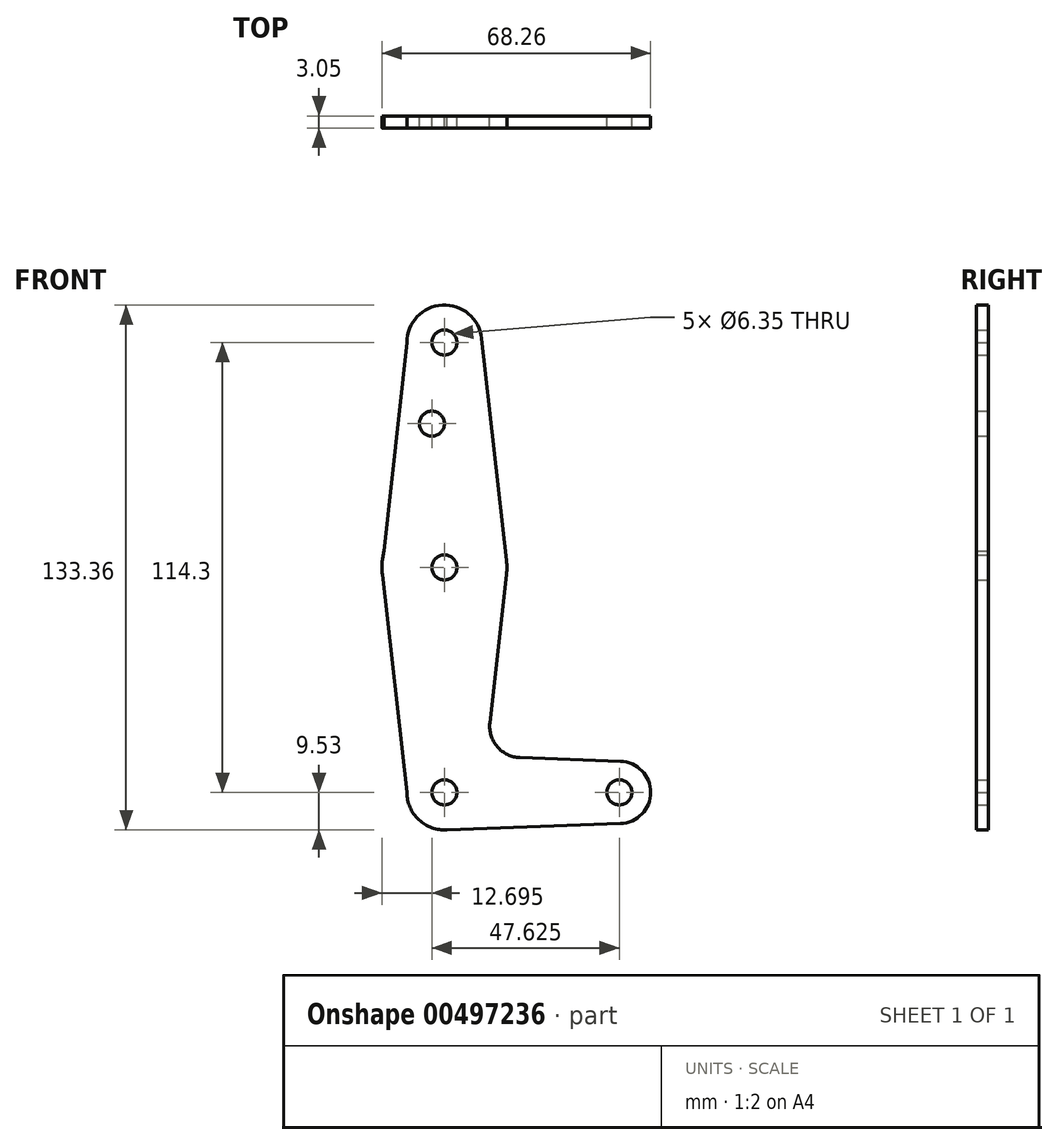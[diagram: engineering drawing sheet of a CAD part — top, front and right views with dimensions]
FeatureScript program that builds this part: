
annotation { "Feature Type Name" : "Feature", "Feature Type Description" : "" }
export const myFeature = defineFeature(function(context is Context, id is Id, definition is map)
    precondition{}
    {
        {
            var Q0;
            Q0=qCreatedBy(makeId("Front.planeOp"),FACE);
            var sketch = newSketch(context, id + "F0", { "sketchPlane" : qUnion([Q0])});
            skLineSegment(sketch, "E0", {"start": v(0, 0) * mm, "end": v(0, 114.3) * mm});
            skLineSegment(sketch, "E1", {"start": v(0, 0) * mm, "end": v(44.45, 0) * mm});
            skCircle(sketch, "E2", {"center": v(0, 0) * mm, "radius": 9.53 * mm});
            skCircle(sketch, "E3", {"center": v(44.45, 0) * mm, "radius": 7.94 * mm});
            skCircle(sketch, "E4", {"center": v(0, 57.15) * mm, "radius": 15.88 * mm});
            skCircle(sketch, "E5", {"center": v(0, 114.3) * mm, "radius": 9.53 * mm});
            skLineSegment(sketch, "E6", {"start": v(0, -9.53) * mm, "end": v(44.73, -7.93) * mm});
            skLineSegment(sketch, "E7", {"start": v(19.18, 8.84) * mm, "end": v(44.73, 7.93) * mm});
            skLineSegment(sketch, "E8", {"start": v(15.78, 55.39) * mm, "end": v(11.56, 17.67) * mm});
            skLineSegment(sketch, "E9", {"start": v(15.78, 58.91) * mm, "end": v(9.47, 115.36) * mm});
            skLineSegment(sketch, "E10", {"start": v(-15.77, 55.37) * mm, "end": v(-9.52, 0) * mm});
            skCircle(sketch, "E11", {"center": v(0, 114.3) * mm, "radius": 3.18 * mm});
            skCircle(sketch, "E12", {"center": v(0, 57.15) * mm, "radius": 3.18 * mm});
            skCircle(sketch, "E13", {"center": v(-3.18, 93.68) * mm, "radius": 3.18 * mm});
            skCircle(sketch, "E14", {"center": v(44.45, 0) * mm, "radius": 3.18 * mm});
            skCircle(sketch, "E15", {"center": v(0, 0) * mm, "radius": 3.18 * mm});
            skLineSegment(sketch, "E16", {"start": v(-15.77, 57.15) * mm, "end": v(-9.52, 114.3) * mm});
            skArc(sketch, "E17.filletArc", {"start": v(11.56, 17.67) * mm, "mid": v(13.44, 11.6) * mm, "end": v(19.18, 8.84) * mm});
            skSolve(sketch);
        }
        {
            var Q0;
            Q0 = qSketchRegion(id + "F0", true);
            var Q1;
            {var subQ0=sQuery(id+"F0.wireOp",EDGE,"E15");var subQ1=sQuery(id+"F0.wireOp",EDGE,"E0");var subQ2=makeQuery(id+"F0.imprint","INTERSECT",VERTEX,{"derivedFrom":[subQ1,subQ0]});Q1=makeQuery(id+"F0.imprint","IMPRINT",FACE,{"disambiguationData":[TD([[makeQuery(id+"F0.imprint","IMPRINT",EDGE,{"disambiguationData":[TD([[subQ2,-1.0]])],"derivedFrom":subQ1}),-1.0]])]});}
            extrude(context, id + "F1", {"entities" : qUnion([Q0, Q1]), "depth" : 3.05 * mm});
        }
    });
